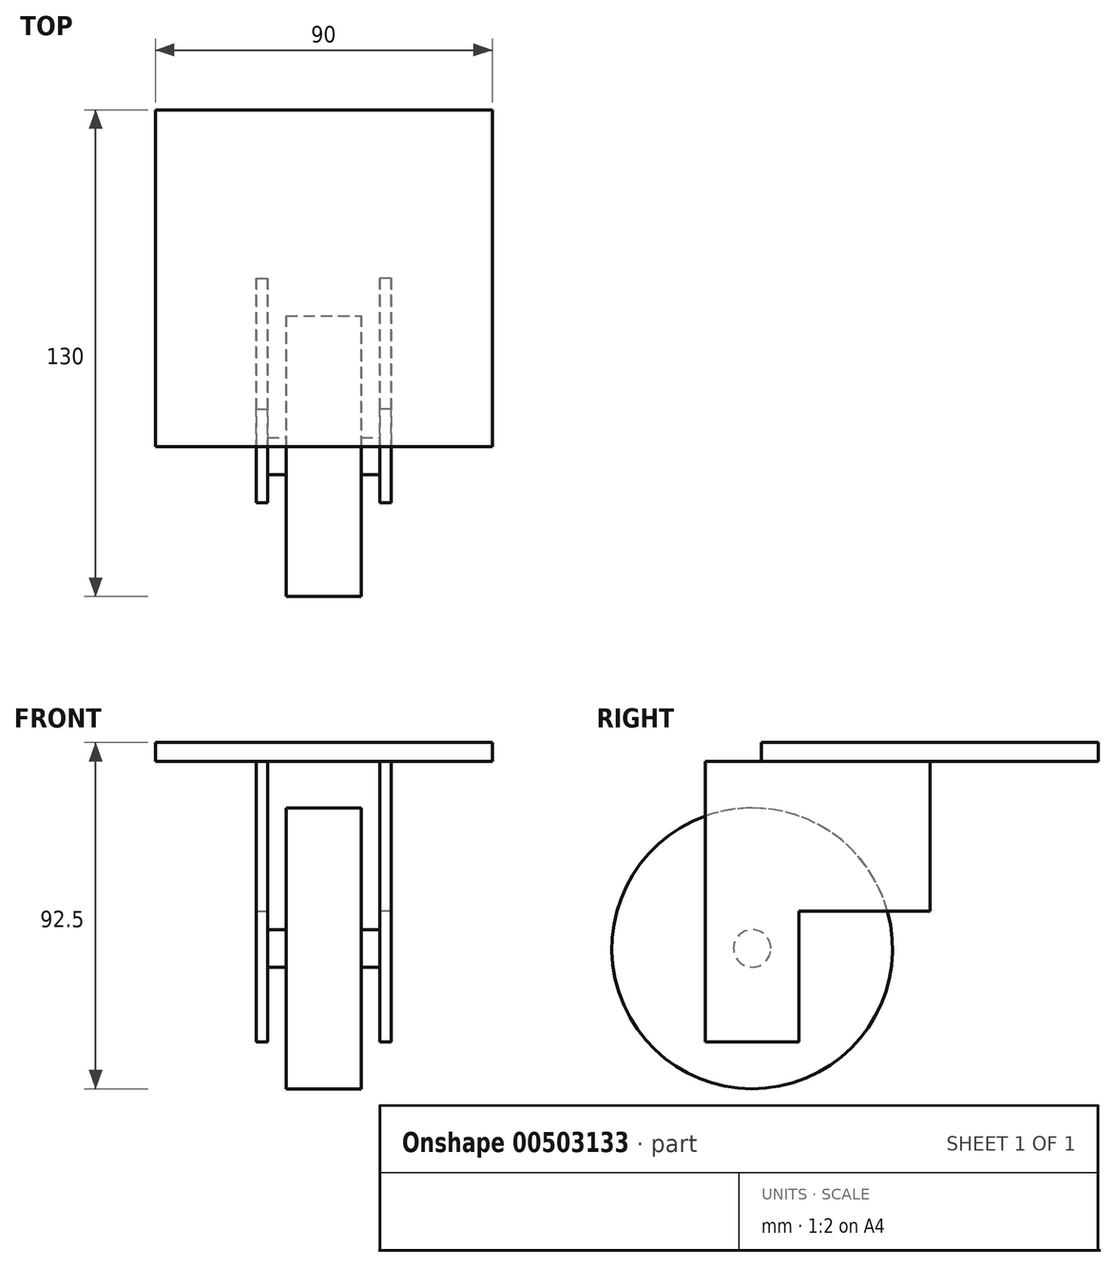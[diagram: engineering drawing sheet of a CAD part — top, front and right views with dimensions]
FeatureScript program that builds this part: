
annotation { "Feature Type Name" : "Feature", "Feature Type Description" : "" }
export const myFeature = defineFeature(function(context is Context, id is Id, definition is map)
    precondition{}
    {
        {
            var Q0;
            Q0=qCreatedBy(makeId("Right.planeOp"),FACE);
            var sketch = newSketch(context, id + "F0", { "sketchPlane" : qUnion([Q0])});
            skLineSegment(sketch, "E0", {"start": v(-12.5, -25) * mm, "end": v(12.5, -25) * mm});
            skLineSegment(sketch, "E1", {"start": v(12.5, -25) * mm, "end": v(12.5, 10) * mm});
            skLineSegment(sketch, "E2", {"start": v(12.5, 10) * mm, "end": v(47.5, 10) * mm});
            skLineSegment(sketch, "E3", {"start": v(47.5, 10) * mm, "end": v(47.5, 50) * mm});
            skLineSegment(sketch, "E4", {"start": v(47.5, 50) * mm, "end": v(-12.5, 50) * mm});
            skLineSegment(sketch, "E5", {"start": v(-12.5, 50) * mm, "end": v(-12.5, -25) * mm});
            skSolve(sketch);
        }
        {
            var Q0;
            Q0 = qSketchRegion(id + "F0", true);
            extrude(context, id + "F1", {"entities" : qUnion([Q0]), "depth" : 3 * mm, "offsetDistance" : 25 * mm});
        }
        {
            var Q0;
            Q0=makeQuery(id+"F1.opExtrude","CAP_FACE",FACE,{"disambiguationData":[OSD([sQuery(id+"F0.wireOp",EDGE,"E0"),sQuery(id+"F0.wireOp",EDGE,"E1"),sQuery(id+"F0.wireOp",EDGE,"E2"),sQuery(id+"F0.wireOp",EDGE,"E3"),sQuery(id+"F0.wireOp",EDGE,"E4"),sQuery(id+"F0.wireOp",EDGE,"E5")])],"isStart":true});
            var sketch = newSketch(context, id + "F2", { "sketchPlane" : qUnion([Q0])});
            skCircle(sketch, "E6", {"center": v(0, 0) * mm, "radius": 5 * mm});
            skSolve(sketch);
        }
        {
            var Q0;
            Q0 = qSketchRegion(id + "F2", true);
            extrude(context, id + "F3", {"entities" : qUnion([Q0]), "operationType" : NewBodyOperationType.ADD, "depth" : 5 * mm, "offsetDistance" : 25 * mm});
        }
        {
            var Q0;
            Q0=makeQuery(id+"F3.opExtrude","CAP_FACE",FACE,{"disambiguationData":[OSD([sQuery(id+"F2.wireOp",EDGE,"E6")])],"isStart":false});
            var sketch = newSketch(context, id + "F4", { "sketchPlane" : qUnion([Q0])});
            skCircle(sketch, "E7", {"center": v(0, 0) * mm, "radius": 37.5 * mm});
            skSolve(sketch);
        }
        {
            var Q0;
            Q0 = qSketchRegion(id + "F4", true);
            extrude(context, id + "F5", {"entities" : qUnion([Q0]), "operationType" : NewBodyOperationType.ADD, "depth" : 20 * mm, "offsetDistance" : 25 * mm});
        }
        {
            var Q0;
            Q0=makeQuery(id+"F5.opExtrude","CAP_FACE",FACE,{"disambiguationData":[OSD([sQuery(id+"F4.wireOp",EDGE,"E7")])],"isStart":false});
            var sketch = newSketch(context, id + "F6", { "sketchPlane" : qUnion([Q0])});
            skCircle(sketch, "E8", {"center": v(0, 0) * mm, "radius": 5 * mm});
            skSolve(sketch);
        }
        {
            var Q0;
            Q0 = qSketchRegion(id + "F6", true);
            extrude(context, id + "F7", {"entities" : qUnion([Q0]), "operationType" : NewBodyOperationType.ADD, "depth" : 5 * mm, "offsetDistance" : 25 * mm});
        }
        {
            var Q0;
            Q0=makeQuery(id+"F7.opExtrude","CAP_FACE",FACE,{"disambiguationData":[OSD([sQuery(id+"F6.wireOp",EDGE,"E8")])],"isStart":false});
            var sketch = newSketch(context, id + "F8", { "sketchPlane" : qUnion([Q0])});
            skLineSegment(sketch, "E9", {"start": v(-47.5, 50) * mm, "end": v(12.5, 50) * mm});
            skLineSegment(sketch, "E10", {"start": v(12.5, 50) * mm, "end": v(12.5, -25) * mm});
            skLineSegment(sketch, "E11", {"start": v(12.5, -25) * mm, "end": v(-12.5, -25) * mm});
            skLineSegment(sketch, "E12", {"start": v(-12.5, -25) * mm, "end": v(-12.5, 10) * mm});
            skLineSegment(sketch, "E13", {"start": v(-12.5, 10) * mm, "end": v(-47.5, 10) * mm});
            skLineSegment(sketch, "E14", {"start": v(-47.5, 10) * mm, "end": v(-47.5, 50) * mm});
            skSolve(sketch);
        }
        {
            var Q0;
            Q0 = qSketchRegion(id + "F8", true);
            extrude(context, id + "F9", {"entities" : qUnion([Q0]), "operationType" : NewBodyOperationType.ADD, "depth" : 3 * mm, "offsetDistance" : 25 * mm});
        }
        {
            var Q0;
            Q0=makeQuery(id+"F9.opExtrude","SWEPT_FACE",FACE,{"disambiguationData":[OSD([sQuery(id+"F8.wireOp",EDGE,"E9")])]});
            var sketch = newSketch(context, id + "F10", { "sketchPlane" : qUnion([Q0])});
            skLineSegment(sketch, "E15.bottom", {"start": v(-60, 92.5) * mm, "end": v(30, 92.5) * mm});
            skLineSegment(sketch, "E15.top", {"start": v(-60, 2.5) * mm, "end": v(30, 2.5) * mm});
            skLineSegment(sketch, "E15.left", {"start": v(-60, 92.5) * mm, "end": v(-60, 2.5) * mm});
            skLineSegment(sketch, "E15.right", {"start": v(30, 92.5) * mm, "end": v(30, 2.5) * mm});
            skSolve(sketch);
        }
        {
            var Q0;
            Q0 = qSketchRegion(id + "F10", true);
            extrude(context, id + "F11", {"entities" : qUnion([Q0]), "operationType" : NewBodyOperationType.ADD, "depth" : 5 * mm, "offsetDistance" : 25 * mm});
        }
    });
